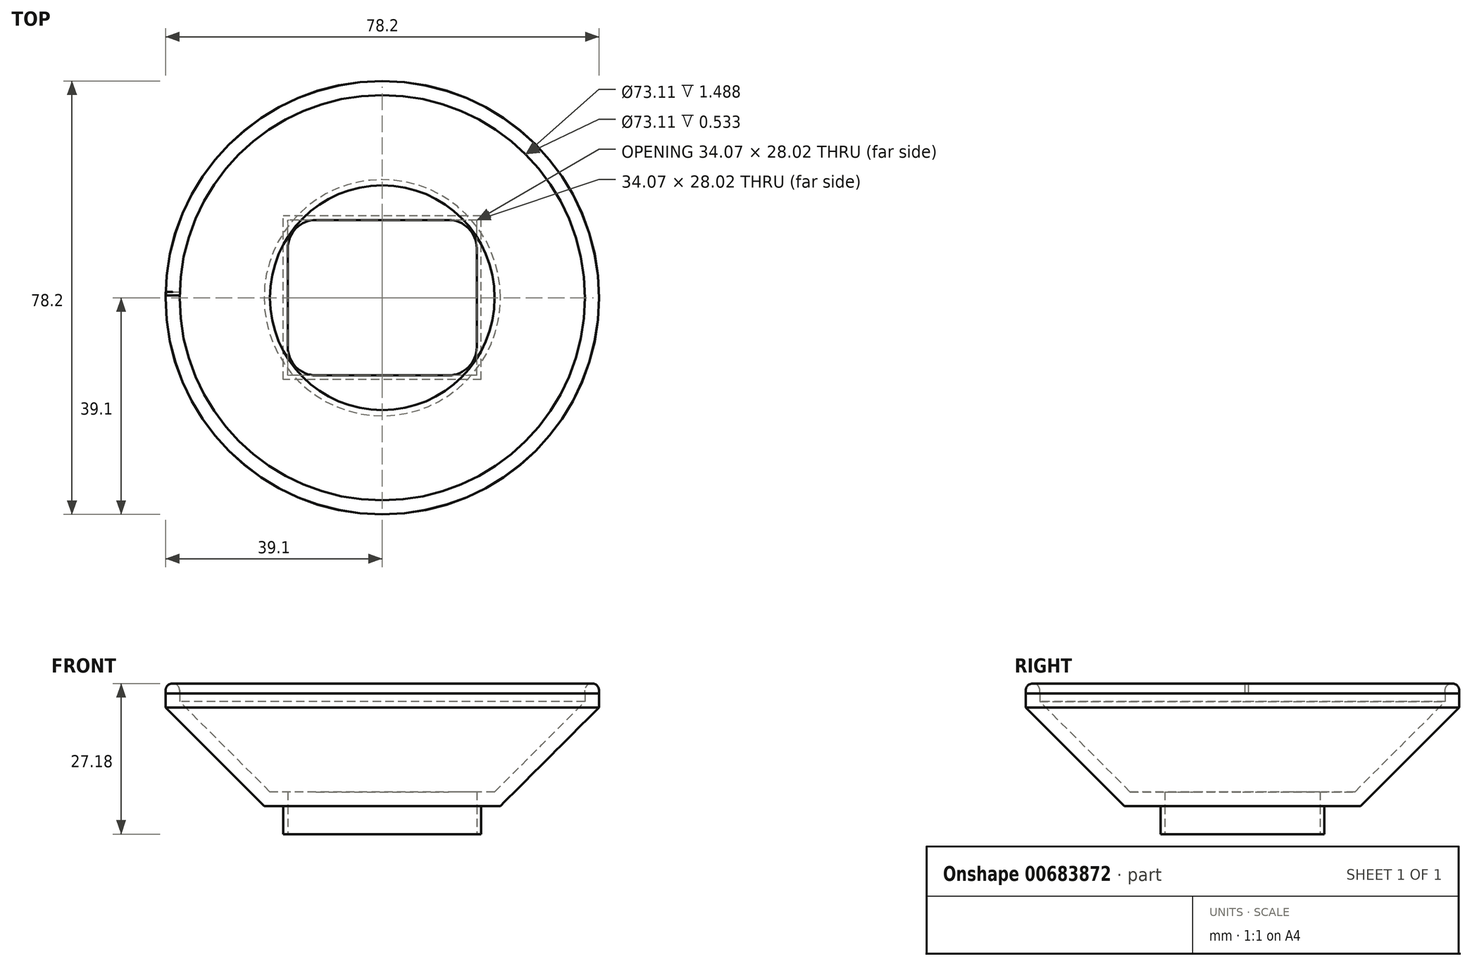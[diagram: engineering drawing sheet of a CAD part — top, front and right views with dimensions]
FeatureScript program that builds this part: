
annotation { "Feature Type Name" : "Feature", "Feature Type Description" : "" }
export const myFeature = defineFeature(function(context is Context, id is Id, definition is map)
    precondition{}
    {
        {
            var Q0;
            Q0=qCreatedBy(makeId("Top.planeOp"),FACE);
            var sketch = newSketch(context, id + "F0", { "sketchPlane" : qUnion([Q0])});
            skLineSegment(sketch, "E0.bottom", {"start": v(17.04, -14.01) * mm, "end": v(-17.04, -14.01) * mm});
            skLineSegment(sketch, "E0.top", {"start": v(17.04, 14.01) * mm, "end": v(-17.04, 14.01) * mm});
            skLineSegment(sketch, "E0.left", {"start": v(17.04, -14.01) * mm, "end": v(17.04, 14.01) * mm});
            skLineSegment(sketch, "E0.right", {"start": v(-17.04, -14.01) * mm, "end": v(-17.04, 14.01) * mm});
            skPoint(sketch, "E0.middle", {"position": v(0, 0) * mm});
            skLineSegment(sketch, "E1.bottom", {"start": v(17.84, -14.8) * mm, "end": v(-17.84, -14.8) * mm});
            skLineSegment(sketch, "E1.top", {"start": v(17.84, 14.8) * mm, "end": v(-17.84, 14.8) * mm});
            skLineSegment(sketch, "E1.left", {"start": v(17.84, -14.8) * mm, "end": v(17.84, 14.8) * mm});
            skLineSegment(sketch, "E1.right", {"start": v(-17.84, -14.8) * mm, "end": v(-17.84, 14.8) * mm});
            skSolve(sketch);
        }
        {
            var Q0;
            Q0=makeQuery(id+"F0.imprint","IMPRINT",FACE,{"disambiguationData":[TD([[makeQuery(id+"F0.imprint","IMPRINT",EDGE,{"derivedFrom":sQuery(id+"F0.wireOp",EDGE,"E0.bottom")}),1.0]])]});
            extrude(context, id + "F1", {"entities" : qUnion([Q0]), "depth" : 2.54 * mm, "offsetDistance" : 25.4 * mm, "hasSecondDirection" : true, "secondDirectionOppositeDirection" : true, "secondDirectionDepth" : 2.54 * mm});
        }
        {
            var Q0;
            Q0=makeQuery(id+"F1.opExtrude","CAP_FACE",FACE,{"disambiguationData":[OSD([sQuery(id+"F0.wireOp",EDGE,"E0.bottom"),sQuery(id+"F0.wireOp",EDGE,"E0.top"),sQuery(id+"F0.wireOp",EDGE,"E0.left"),sQuery(id+"F0.wireOp",EDGE,"E0.right"),sQuery(id+"F0.wireOp",EDGE,"E1.bottom"),sQuery(id+"F0.wireOp",EDGE,"E1.top"),sQuery(id+"F0.wireOp",EDGE,"E1.left"),sQuery(id+"F0.wireOp",EDGE,"E1.right")])],"isStart":false});
            var sketch = newSketch(context, id + "F2", { "sketchPlane" : qUnion([Q0])});
            skCircle(sketch, "E2", {"center": v(0, 0) * mm, "radius": 23.18 * mm});
            skCircle(sketch, "E3", {"center": v(0, 0) * mm, "radius": 39.1 * mm});
            skSolve(sketch);
        }
        {
            var Q0;
            {var subQ0=sQuery(id+"F2.wireOp",EDGE,"YeDiYnUJ-6faf-CMuh-WqDV-JdC3Ef2yiBRM");var subQ1=makeQuery(id+"F1.opExtrude","CAP_EDGE",EDGE,{"disambiguationData":[OSD([sQuery(id+"F0.wireOp",EDGE,"E1.right")])],"isStart":false});var subQ2=makeQuery(id+"F2.imprint","INTERSECT",VERTEX,{"disambiguationData":[OD(0.0)],"derivedFrom":[subQ1,subQ0]});Q0=makeQuery(id+"F2.imprint","IMPRINT",FACE,{"disambiguationData":[TD([[makeQuery(id+"F2.imprint","IMPRINT",EDGE,{"disambiguationData":[TD([[subQ2,-1.0]])],"derivedFrom":subQ0}),-1.0]])]});}
            var Q1;
            {var subQ0=sQuery(id+"F2.wireOp",EDGE,"YeDiYnUJ-6faf-CMuh-WqDV-JdC3Ef2yiBRM");var subQ2=makeQuery(id+"F1.opExtrude","CAP_EDGE",EDGE,{"disambiguationData":[OSD([sQuery(id+"F0.wireOp",EDGE,"E1.right")])],"isStart":false});var subQ3=makeQuery(id+"F2.imprint","INTERSECT",VERTEX,{"disambiguationData":[OD(1.0)],"derivedFrom":[subQ2,subQ0]});Q1=makeQuery(id+"F2.imprint","IMPRINT",FACE,{"disambiguationData":[TD([[makeQuery(id+"F2.imprint","IMPRINT",EDGE,{"disambiguationData":[TD([[subQ3,-1.0]])],"derivedFrom":subQ0}),-1.0]])]});}
            var Q2;
            {var subQ0=sQuery(id+"F2.wireOp",EDGE,"YeDiYnUJ-6faf-CMuh-WqDV-JdC3Ef2yiBRM");var subQ1=makeQuery(id+"F1.opExtrude","CAP_EDGE",EDGE,{"disambiguationData":[OSD([sQuery(id+"F0.wireOp",EDGE,"E1.bottom")])],"isStart":false});var subQ2=makeQuery(id+"F2.imprint","INTERSECT",VERTEX,{"disambiguationData":[OD(0.0)],"derivedFrom":[subQ1,subQ0]});Q2=makeQuery(id+"F2.imprint","IMPRINT",FACE,{"disambiguationData":[TD([[makeQuery(id+"F2.imprint","IMPRINT",EDGE,{"disambiguationData":[TD([[subQ2,-1.0]])],"derivedFrom":subQ0}),-1.0]])]});}
            var Q3;
            {var subQ0=sQuery(id+"F2.wireOp",EDGE,"YeDiYnUJ-6faf-CMuh-WqDV-JdC3Ef2yiBRM");var subQ2=makeQuery(id+"F1.opExtrude","CAP_EDGE",EDGE,{"disambiguationData":[OSD([sQuery(id+"F0.wireOp",EDGE,"E1.bottom")])],"isStart":false});var subQ3=makeQuery(id+"F2.imprint","INTERSECT",VERTEX,{"disambiguationData":[OD(1.0)],"derivedFrom":[subQ2,subQ0]});Q3=makeQuery(id+"F2.imprint","IMPRINT",FACE,{"disambiguationData":[TD([[makeQuery(id+"F2.imprint","IMPRINT",EDGE,{"disambiguationData":[TD([[subQ3,-1.0]])],"derivedFrom":subQ0}),-1.0]])]});}
            var Q4;
            {var subQ0=sQuery(id+"F2.wireOp",EDGE,"YeDiYnUJ-6faf-CMuh-WqDV-JdC3Ef2yiBRM");var subQ1=makeQuery(id+"F1.opExtrude","CAP_EDGE",EDGE,{"disambiguationData":[OSD([sQuery(id+"F0.wireOp",EDGE,"E1.left")])],"isStart":false});var subQ2=makeQuery(id+"F2.imprint","INTERSECT",VERTEX,{"disambiguationData":[OD(0.0)],"derivedFrom":[subQ1,subQ0]});Q4=makeQuery(id+"F2.imprint","IMPRINT",FACE,{"disambiguationData":[TD([[makeQuery(id+"F2.imprint","IMPRINT",EDGE,{"disambiguationData":[TD([[subQ2,1.0]])],"derivedFrom":subQ0}),-1.0]])]});}
            var Q5;
            {var subQ0=sQuery(id+"F2.wireOp",EDGE,"YeDiYnUJ-6faf-CMuh-WqDV-JdC3Ef2yiBRM");var subQ2=makeQuery(id+"F1.opExtrude","CAP_EDGE",EDGE,{"disambiguationData":[OSD([sQuery(id+"F0.wireOp",EDGE,"E1.left")])],"isStart":false});var subQ3=makeQuery(id+"F2.imprint","INTERSECT",VERTEX,{"disambiguationData":[OD(0.0)],"derivedFrom":[subQ2,subQ0]});Q5=makeQuery(id+"F2.imprint","IMPRINT",FACE,{"disambiguationData":[TD([[makeQuery(id+"F2.imprint","IMPRINT",EDGE,{"disambiguationData":[TD([[subQ3,-1.0]])],"derivedFrom":subQ0}),-1.0]])]});}
            var Q6;
            {var subQ0=sQuery(id+"F2.wireOp",EDGE,"YeDiYnUJ-6faf-CMuh-WqDV-JdC3Ef2yiBRM");var subQ1=makeQuery(id+"F1.opExtrude","CAP_EDGE",EDGE,{"disambiguationData":[OSD([sQuery(id+"F0.wireOp",EDGE,"E1.top")])],"isStart":false});var subQ2=makeQuery(id+"F2.imprint","INTERSECT",VERTEX,{"disambiguationData":[OD(0.0)],"derivedFrom":[subQ1,subQ0]});Q6=makeQuery(id+"F2.imprint","IMPRINT",FACE,{"disambiguationData":[TD([[makeQuery(id+"F2.imprint","IMPRINT",EDGE,{"disambiguationData":[TD([[subQ2,-1.0]])],"derivedFrom":subQ0}),-1.0]])]});}
            var Q7;
            {var subQ0=sQuery(id+"F2.wireOp",EDGE,"YeDiYnUJ-6faf-CMuh-WqDV-JdC3Ef2yiBRM");var subQ2=makeQuery(id+"F1.opExtrude","CAP_EDGE",EDGE,{"disambiguationData":[OSD([sQuery(id+"F0.wireOp",EDGE,"E1.top")])],"isStart":false});var subQ3=makeQuery(id+"F2.imprint","INTERSECT",VERTEX,{"disambiguationData":[OD(1.0)],"derivedFrom":[subQ2,subQ0]});Q7=makeQuery(id+"F2.imprint","IMPRINT",FACE,{"disambiguationData":[TD([[makeQuery(id+"F2.imprint","IMPRINT",EDGE,{"disambiguationData":[TD([[subQ3,-1.0]])],"derivedFrom":subQ0}),-1.0]])]});}
            var Q8;
            {var subQ0=sQuery(id+"F2.wireOp",EDGE,"YeDiYnUJ-6faf-CMuh-WqDV-JdC3Ef2yiBRM");var subQ1=makeQuery(id+"F1.opExtrude","CAP_EDGE",EDGE,{"disambiguationData":[OSD([sQuery(id+"F0.wireOp",EDGE,"E1.right")])],"isStart":false});var subQ2=makeQuery(id+"F2.imprint","INTERSECT",VERTEX,{"disambiguationData":[OD(0.0)],"derivedFrom":[subQ1,subQ0]});Q8=makeQuery(id+"F2.imprint","IMPRINT",FACE,{"disambiguationData":[TD([[makeQuery(id+"F2.imprint","IMPRINT",EDGE,{"disambiguationData":[TD([[subQ2,-1.0]])],"derivedFrom":subQ0}),1.0]])]});}
            var Q9;
            {var subQ0=sQuery(id+"F2.wireOp",EDGE,"YeDiYnUJ-6faf-CMuh-WqDV-JdC3Ef2yiBRM");var subQ1=makeQuery(id+"F1.opExtrude","CAP_EDGE",EDGE,{"disambiguationData":[OSD([sQuery(id+"F0.wireOp",EDGE,"E1.top")])],"isStart":false});var subQ2=makeQuery(id+"F2.imprint","INTERSECT",VERTEX,{"disambiguationData":[OD(0.0)],"derivedFrom":[subQ1,subQ0]});Q9=makeQuery(id+"F2.imprint","IMPRINT",FACE,{"disambiguationData":[TD([[makeQuery(id+"F2.imprint","IMPRINT",EDGE,{"disambiguationData":[TD([[subQ2,-1.0]])],"derivedFrom":subQ0}),1.0]])]});}
            var Q10;
            {var subQ0=sQuery(id+"F2.wireOp",EDGE,"YeDiYnUJ-6faf-CMuh-WqDV-JdC3Ef2yiBRM");var subQ1=makeQuery(id+"F1.opExtrude","CAP_EDGE",EDGE,{"disambiguationData":[OSD([sQuery(id+"F0.wireOp",EDGE,"E1.bottom")])],"isStart":false});var subQ2=makeQuery(id+"F2.imprint","INTERSECT",VERTEX,{"disambiguationData":[OD(0.0)],"derivedFrom":[subQ1,subQ0]});Q10=makeQuery(id+"F2.imprint","IMPRINT",FACE,{"disambiguationData":[TD([[makeQuery(id+"F2.imprint","IMPRINT",EDGE,{"disambiguationData":[TD([[subQ2,-1.0]])],"derivedFrom":subQ0}),1.0]])]});}
            var Q11;
            {var subQ0=sQuery(id+"F2.wireOp",EDGE,"YeDiYnUJ-6faf-CMuh-WqDV-JdC3Ef2yiBRM");var subQ1=makeQuery(id+"F1.opExtrude","CAP_EDGE",EDGE,{"disambiguationData":[OSD([sQuery(id+"F0.wireOp",EDGE,"E1.left")])],"isStart":false});var subQ2=makeQuery(id+"F2.imprint","INTERSECT",VERTEX,{"disambiguationData":[OD(0.0)],"derivedFrom":[subQ1,subQ0]});Q11=makeQuery(id+"F2.imprint","IMPRINT",FACE,{"disambiguationData":[TD([[makeQuery(id+"F2.imprint","IMPRINT",EDGE,{"disambiguationData":[TD([[subQ2,1.0]])],"derivedFrom":subQ0}),1.0]])]});}
            var Q12;
            {var subQ1=makeQuery(id+"F1.opExtrude","CAP_EDGE",EDGE,{"disambiguationData":[OSD([sQuery(id+"F0.wireOp",EDGE,"E0.right")])],"isStart":false});Q12=makeQuery(id+"F2.imprint","IMPRINT",FACE,{"disambiguationData":[TD([[makeQuery(id+"F2.imprint","IMPRINT",EDGE,{"derivedFrom":subQ1}),1.0]])]});}
            var Q13;
            {var subQ1=makeQuery(id+"F1.opExtrude","CAP_EDGE",EDGE,{"disambiguationData":[OSD([sQuery(id+"F0.wireOp",EDGE,"E0.bottom")])],"isStart":false});Q13=makeQuery(id+"F2.imprint","IMPRINT",FACE,{"disambiguationData":[TD([[makeQuery(id+"F2.imprint","IMPRINT",EDGE,{"derivedFrom":subQ1}),1.0]])]});}
            var Q14;
            {var subQ1=makeQuery(id+"F1.opExtrude","CAP_EDGE",EDGE,{"disambiguationData":[OSD([sQuery(id+"F0.wireOp",EDGE,"E0.left")])],"isStart":false});Q14=makeQuery(id+"F2.imprint","IMPRINT",FACE,{"disambiguationData":[TD([[makeQuery(id+"F2.imprint","IMPRINT",EDGE,{"derivedFrom":subQ1}),-1.0]])]});}
            var Q15;
            {var subQ1=makeQuery(id+"F1.opExtrude","CAP_EDGE",EDGE,{"disambiguationData":[OSD([sQuery(id+"F0.wireOp",EDGE,"E0.top")])],"isStart":false});Q15=makeQuery(id+"F2.imprint","IMPRINT",FACE,{"disambiguationData":[TD([[makeQuery(id+"F2.imprint","IMPRINT",EDGE,{"derivedFrom":subQ1}),-1.0]])]});}
            var Q16;
            Q16=makeQuery(id+"F2.imprint","IMPRINT",FACE,{"disambiguationData":[TD([[makeQuery(id+"F2.imprint","IMPRINT",EDGE,{"derivedFrom":makeQuery(id+"F1.opExtrude","CAP_EDGE",EDGE,{"disambiguationData":[OSD([sQuery(id+"F0.wireOp",EDGE,"E0.bottom")])],"isStart":false})}),-1.0]])]});
            var Q17;
            {var subQ1=makeQuery(id+"F1.opExtrude","CAP_EDGE",EDGE,{"disambiguationData":[OSD([sQuery(id+"F0.wireOp",EDGE,"E1.bottom")])],"isStart":false});Q17=makeQuery(id+"F2.imprint","IMPRINT",FACE,{"disambiguationData":[TD([[makeQuery(id+"F2.imprint","IMPRINT",EDGE,{"derivedFrom":subQ1}),1.0]])]});}
            var Q18;
            {var subQ1=makeQuery(id+"F1.opExtrude","CAP_EDGE",EDGE,{"disambiguationData":[OSD([sQuery(id+"F0.wireOp",EDGE,"E1.right")])],"isStart":false});Q18=makeQuery(id+"F2.imprint","IMPRINT",FACE,{"disambiguationData":[TD([[makeQuery(id+"F2.imprint","IMPRINT",EDGE,{"derivedFrom":subQ1}),1.0]])]});}
            var Q19;
            {var subQ1=makeQuery(id+"F1.opExtrude","CAP_EDGE",EDGE,{"disambiguationData":[OSD([sQuery(id+"F0.wireOp",EDGE,"E1.top")])],"isStart":false});Q19=makeQuery(id+"F2.imprint","IMPRINT",FACE,{"disambiguationData":[TD([[makeQuery(id+"F2.imprint","IMPRINT",EDGE,{"derivedFrom":subQ1}),-1.0]])]});}
            var Q20;
            {var subQ1=makeQuery(id+"F1.opExtrude","CAP_EDGE",EDGE,{"disambiguationData":[OSD([sQuery(id+"F0.wireOp",EDGE,"E1.left")])],"isStart":false});Q20=makeQuery(id+"F2.imprint","IMPRINT",FACE,{"disambiguationData":[TD([[makeQuery(id+"F2.imprint","IMPRINT",EDGE,{"derivedFrom":subQ1}),-1.0]])]});}
            var Q21;
            Q21=makeQuery(id+"F2.imprint","IMPRINT",FACE,{"disambiguationData":[TD([[makeQuery(id+"F2.imprint","IMPRINT",EDGE,{"derivedFrom":sQuery(id+"F2.wireOp",EDGE,"E3")}),1.0]])]});
            extrude(context, id + "F3", {"entities" : qUnion([Q0, Q1, Q2, Q3, Q4, Q5, Q6, Q7, Q8, Q9, Q10, Q11, Q12, Q13, Q14, Q15, Q16, Q17, Q18, Q19, Q20, Q21]), "depth" : 20.32 * mm, "offsetDistance" : 25.4 * mm});
        }
        {
            var Q0;
            Q0=makeQuery(id+"F3.opExtrude","CAP_FACE",FACE,{"disambiguationData":[OSD([sQuery(id+"F2.wireOp",EDGE,"E3")])],"isStart":true});
            chamfer(context, id + "F4", {"entities" : qUnion([Q0]), "width" : 17.78 * mm, "tangentPropagation" : true});
        }
        {
            var Q0;
            Q0=makeQuery(id+"F3.opExtrude","CAP_FACE",FACE,{"disambiguationData":[OSD([sQuery(id+"F2.wireOp",EDGE,"E3")])],"isStart":false});
            shell(context, id + "F5", {"entities" : qUnion([Q0]), "thickness" : 2.54 * mm});
        }
        {
            var Q0;
            Q0=makeQuery(id+"F0.imprint","IMPRINT",FACE,{"disambiguationData":[TD([[makeQuery(id+"F0.imprint","IMPRINT",EDGE,{"derivedFrom":sQuery(id+"F0.wireOp",EDGE,"E0.bottom")}),-1.0]])]});
            extrude(context, id + "F6", {"entities" : qUnion([Q0]), "operationType" : NewBodyOperationType.REMOVE, "depth" : 13.2 * mm, "offsetDistance" : 25.4 * mm});
        }
        {
            var Q0;
            Q0=makeQuery(id+"F6.boolean.opBoolean","COPY",EDGE,{"derivedFrom":makeQuery(id+"F6.opExtrude","SWEPT_EDGE",EDGE,{"disambiguationData":[OSD([sQuery(id+"F0.wireOp",EDGE,"E0.top"),sQuery(id+"F0.wireOp",EDGE,"E0.right")])]})});
            var Q1;
            Q1=makeQuery(id+"F6.boolean.opBoolean","COPY",EDGE,{"derivedFrom":makeQuery(id+"F6.opExtrude","SWEPT_EDGE",EDGE,{"disambiguationData":[OSD([sQuery(id+"F0.wireOp",EDGE,"E0.top"),sQuery(id+"F0.wireOp",EDGE,"E0.left")])]})});
            var Q2;
            Q2=makeQuery(id+"F6.boolean.opBoolean","COPY",EDGE,{"derivedFrom":makeQuery(id+"F6.opExtrude","SWEPT_EDGE",EDGE,{"disambiguationData":[OSD([sQuery(id+"F0.wireOp",EDGE,"E0.bottom"),sQuery(id+"F0.wireOp",EDGE,"E0.left")])]})});
            var Q3;
            Q3=makeQuery(id+"F6.boolean.opBoolean","COPY",EDGE,{"derivedFrom":makeQuery(id+"F6.opExtrude","SWEPT_EDGE",EDGE,{"disambiguationData":[OSD([sQuery(id+"F0.wireOp",EDGE,"E0.bottom"),sQuery(id+"F0.wireOp",EDGE,"E0.right")])]})});
            fillet(context, id + "F7", {"entities" : qUnion([Q0, Q1, Q2, Q3]), "radius" : 5.08 * mm, "tangentPropagation" : true, "allowEdgeOverflow" : false});
        }
        {
            var Q0;
            Q0=makeQuery(id+"F3.opExtrude","CAP_FACE",FACE,{"disambiguationData":[OSD([sQuery(id+"F2.wireOp",EDGE,"E3")])],"isStart":false});
            var sketch = newSketch(context, id + "F8", { "sketchPlane" : qUnion([Q0])});
            skLineSegment(sketch, "E4.bottom", {"start": v(-39.08, 1.08) * mm, "end": v(-36.55, 1.08) * mm});
            skLineSegment(sketch, "E4.top", {"start": v(-39.08, 0.43) * mm, "end": v(-36.55, 0.43) * mm});
            skLineSegment(sketch, "E4.left", {"start": v(-39.08, 1.08) * mm, "end": v(-39.08, 0.43) * mm});
            skLineSegment(sketch, "E4.right", {"start": v(-36.55, 1.08) * mm, "end": v(-36.55, 0.43) * mm});
            skSolve(sketch);
        }
        {
            var Q0;
            Q0 = qSketchRegion(id + "F8", true);
            extrude(context, id + "F9", {"entities" : qUnion([Q0]), "depth" : 1.78 * mm, "offsetDistance" : 25.4 * mm});
        }
        {
            var Q0;
            Q0=makeQuery(id+"F9.opExtrude","SWEPT_FACE",FACE,{"disambiguationData":[OSD([sQuery(id+"F8.wireOp",EDGE,"E4.top")])]});
            var Q1;
            {var subQ0=sQuery(id+"F2.wireOp",EDGE,"E3");Q1=makeQuery(id+"F5.opShell","OFFSET_EDGE",EDGE,{"disambiguationData":[OSD([subQ0]),TDD([makeQuery(id+"F3.opExtrude","CAP_EDGE",EDGE,{"disambiguationData":[OSD([subQ0])],"isStart":false})])]});}
            sweep(context, id + "F10", {"profiles" : qUnion([Q0]), "path" : qUnion([Q1])});
        }
        {
            var Q0;
            {var subQ0=sQuery(id+"F8.wireOp",EDGE,"E4.left");var subQ1=sQuery(id+"F8.wireOp",EDGE,"E4.top");var subQ2=sQuery(id+"F2.wireOp",EDGE,"E3");Q0=makeQuery(id+"F10.opSweep","SWEPT_EDGE",EDGE,{"disambiguationData":[OSD([subQ2,subQ1,subQ0]),TDD([makeQuery(id+"F5.opShell","OFFSET_EDGE",EDGE,{"disambiguationData":[OSD([subQ2]),TDD([makeQuery(id+"F3.opExtrude","CAP_EDGE",EDGE,{"disambiguationData":[OSD([subQ2])],"isStart":false})])]}),makeQuery(id+"F9.opExtrude","CAP_VERTEX",VERTEX,{"disambiguationData":[OSD([subQ1,subQ0])],"isStart":false})])]});}
            var Q1;
            {var subQ0=sQuery(id+"F8.wireOp",EDGE,"E4.right");var subQ1=sQuery(id+"F8.wireOp",EDGE,"E4.top");var subQ2=sQuery(id+"F2.wireOp",EDGE,"E3");Q1=makeQuery(id+"F10.opSweep","SWEPT_EDGE",EDGE,{"disambiguationData":[OSD([subQ2,subQ1,subQ0]),TDD([makeQuery(id+"F5.opShell","OFFSET_EDGE",EDGE,{"disambiguationData":[OSD([subQ2]),TDD([makeQuery(id+"F3.opExtrude","CAP_EDGE",EDGE,{"disambiguationData":[OSD([subQ2])],"isStart":false})])]}),makeQuery(id+"F9.opExtrude","CAP_VERTEX",VERTEX,{"disambiguationData":[OSD([subQ2,subQ1,subQ0])],"isStart":false})])]});}
            fillet(context, id + "F11", {"entities" : qUnion([Q0, Q1]), "radius" : 1.24 * mm, "tangentPropagation" : true, "allowEdgeOverflow" : false});
        }
        {
            var Q0;
            Q0=makeQuery(id+"F9.opExtrude","CAP_EDGE",EDGE,{"disambiguationData":[OSD([sQuery(id+"F8.wireOp",EDGE,"E4.left")])],"isStart":false});
            var Q1;
            Q1=makeQuery(id+"F9.opExtrude","CAP_EDGE",EDGE,{"disambiguationData":[OSD([sQuery(id+"F8.wireOp",EDGE,"E4.right")])],"isStart":false});
            fillet(context, id + "F12", {"entities" : qUnion([Q0, Q1]), "radius" : 1.24 * mm, "tangentPropagation" : true, "allowEdgeOverflow" : false});
        }
    });
